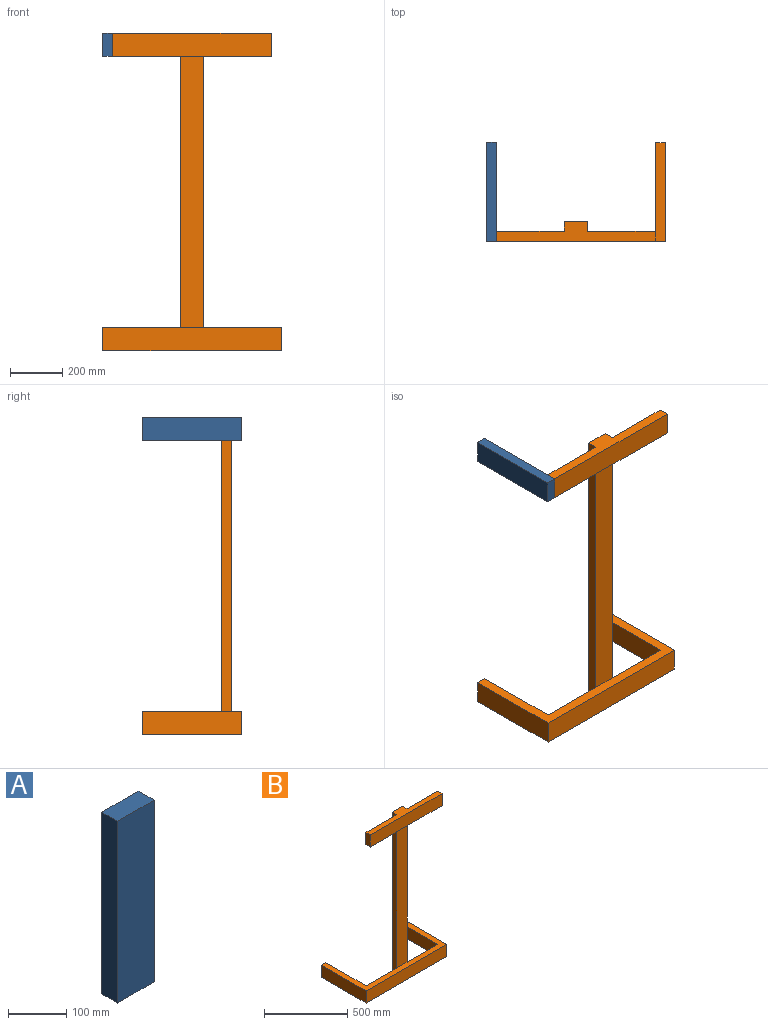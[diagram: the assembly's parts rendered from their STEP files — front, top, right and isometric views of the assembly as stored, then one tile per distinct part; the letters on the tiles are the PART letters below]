
ASSEMBLY  parts=2 mates=1
PART A: 6 faces, bbox 88.9x38.1x381 mm
  f0: plane 381x38.1mm, normal (-1,0,0), area 14516.1mm2, adj f1,f3,f4,f5
  f1: plane 381x88.9mm, normal (0,-1,0), area 33870.9mm2, adj f0,f2,f4,f5
  f2: plane 381x38.1mm, normal (1,0,0), area 14516.1mm2, adj f1,f3,f4,f5
  f3: plane 381x88.9mm, normal (0,1,0), area 33870.9mm2, adj f0,f2,f4,f5
  f4: plane 88.9x38.1mm, normal (0,0,1), area 3387.1mm2, adj f0,f1,f2,f3
  f5: plane 88.9x38.1mm, normal (0,0,-1), area 3387.1mm2, adj f0,f1,f2,f3
PART B: 22 faces, bbox 685.8x381x1219.2 mm
  f0: plane 1219.2x38.1mm, normal (-1,0,0), area 46451.5mm2, adj f1,f3,f4,f5,f6,f10
  f1: plane 1041.4x88.9mm, normal (0,-1,0), area 92580.5mm2, adj f0,f2,f7,f11
  f2: plane 1219.2x38.1mm, normal (1,0,0), area 46451.5mm2, adj f1,f3,f4,f5,f9,f15
  f3: plane 1219.2x88.9mm, normal (0,1,0), area 108386.9mm2, adj f0,f2,f4,f5
  f4: plane 609.6x76.2mm, normal (0,0,1), area 26612.8mm2, adj f0,f2,f3,f10,f12,f13,f14,f15
  f5: plane 685.8x381mm, normal (0,0,-1), area 55645.1mm2, adj f0,f2,f3,f6,f8,f9,f16,f17
  f6: plane 259.33x88.9mm, normal (0,1,0), area 23054.8mm2, adj f0,f5,f7,f16
  f7: plane 685.8x381mm, normal (0,0,1), area 52258mm2, adj f1,f6,f8,f9,f16,f17,f18,f19
  f8: plane 685.8x88.9mm, normal (0,-1,0), area 60967.6mm2, adj f5,f7,f18,f20
  f9: plane 261.37x88.9mm, normal (0,1,0), area 23235.4mm2, adj f2,f5,f7,f21
  f10: plane 260.35x88.9mm, normal (0,1,0), area 23145.1mm2, adj f0,f4,f11,f13
  f11: plane 609.6x38.1mm, normal (0,0,-1), area 23225.8mm2, adj f1,f10,f12,f13,f14,f15
  f12: plane 88.9x38.1mm, normal (1,0,0), area 3387.1mm2, adj f4,f11,f14,f15
  f13: plane 88.9x38.1mm, normal (-1,0,0), area 3387.1mm2, adj f4,f10,f11,f14
  f14: plane 609.6x88.9mm, normal (0,-1,0), area 54193.4mm2, adj f4,f11,f12,f13
  f15: plane 260.35x88.9mm, normal (0,1,0), area 23145.1mm2, adj f2,f4,f11,f12
  f16: plane 342.9x88.9mm, normal (1,0,0), area 30483.8mm2, adj f5,f6,f7,f17
  f17: plane 88.9x38.1mm, normal (0,1,0), area 3387.1mm2, adj f5,f7,f16,f18
  f18: plane 381x88.9mm, normal (-1,0,0), area 33870.9mm2, adj f5,f7,f8,f17
  f19: plane 88.9x38.1mm, normal (0,1,0), area 3387.1mm2, adj f5,f7,f20,f21
  f20: plane 381x88.9mm, normal (1,0,0), area 33870.9mm2, adj f5,f7,f8,f19
  f21: plane 342.9x88.9mm, normal (-1,0,0), area 30483.8mm2, adj f5,f7,f9,f19
PLACE A rot(axis=(-0.58,-0.58,-0.58),120deg) t=(-342.9,-38.1,520.7)mm
PLACE B t=(-44.45,0,-609.6)mm
MATE fastened A.f3 <-> B.f13  axis (1,0,0) through (-304.8,152.4,565.15)mm
